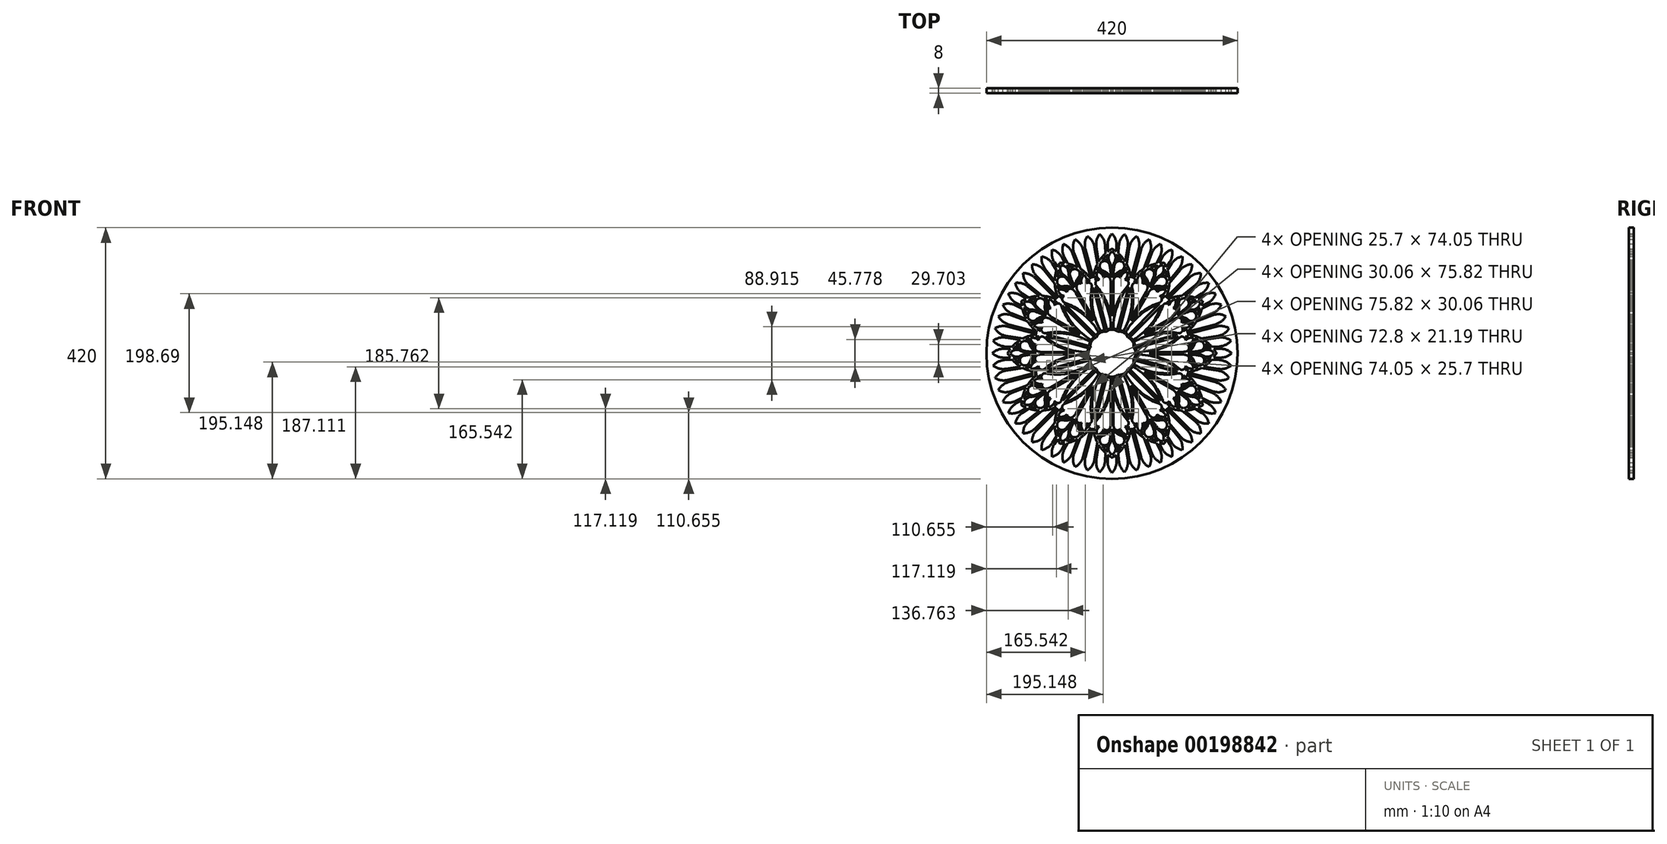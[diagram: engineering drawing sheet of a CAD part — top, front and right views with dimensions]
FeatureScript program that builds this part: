
annotation { "Feature Type Name" : "Feature", "Feature Type Description" : "" }
export const myFeature = defineFeature(function(context is Context, id is Id, definition is map)
    precondition{}
    {
        {
            var Q0;
            Q0=qCreatedBy(makeId("Front.planeOp"),FACE);
            var sketch = newSketch(context, id + "F0", { "sketchPlane" : qUnion([Q0])});
            skLineSegment(sketch, "E0", {"start": v(0, 0) * mm, "end": v(58.1, 216.81) * mm, "construction": true});
            skLineSegment(sketch, "E1", {"start": v(-11.54, 220.15) * mm, "end": v(-2.06, 39.35) * mm, "construction": true});
            skLineSegment(sketch, "E2", {"start": v(0, 220.15) * mm, "end": v(0, 0) * mm, "construction": true});
            skLineSegment(sketch, "E3", {"start": v(0, 0) * mm, "end": v(-33.6, 212.18) * mm, "construction": true});
            skLineSegment(sketch, "E4", {"start": v(0, 0) * mm, "end": v(-7.9, 37.16) * mm, "construction": true});
            skCircle(sketch, "E5", {"center": v(0, 0) * mm, "radius": 200 * mm, "construction": true});
            skCircle(sketch, "E6", {"center": v(0, 0) * mm, "radius": 180 * mm, "construction": true});
            skLineSegment(sketch, "E7", {"start": v(0, 0) * mm, "end": v(-57.94, 216.22) * mm, "construction": true});
            skCircle(sketch, "E8", {"center": v(0, 0) * mm, "radius": 25 * mm, "construction": true});
            skCircle(sketch, "E9", {"center": v(-21.65, 12.5) * mm, "radius": 12.5 * mm, "construction": true});
            skCircle(sketch, "E10", {"center": v(21.65, 12.5) * mm, "radius": 12.5 * mm, "construction": true});
            skCircle(sketch, "E11", {"center": v(21.65, -12.5) * mm, "radius": 12.5 * mm, "construction": true});
            skCircle(sketch, "E12", {"center": v(0, -25) * mm, "radius": 12.5 * mm, "construction": true});
            skCircle(sketch, "E13", {"center": v(-21.65, -12.5) * mm, "radius": 12.5 * mm, "construction": true});
            skLineSegment(sketch, "E14", {"start": v(-25.79, 103.96) * mm, "end": v(-8.43, 39.18) * mm});
            skArc(sketch, "E15", {"start": v(-6.74, 165.04) * mm, "mid": v(-11.52, 160.5) * mm, "end": v(-15.77, 155.46) * mm});
            skArc(sketch, "E16", {"start": v(0, 174.68) * mm, "mid": v(-3.53, 172.47) * mm, "end": v(-6.9, 170.05) * mm});
            skLineSegment(sketch, "E17", {"start": v(-44.65, 174.37) * mm, "end": v(-31.54, 125.45) * mm});
            skLineSegment(sketch, "E18", {"start": v(-29.15, 177.62) * mm, "end": v(-24.6, 148.94) * mm});
            skArc(sketch, "E19", {"start": v(-41.58, 195.63) * mm, "mid": v(-45.3, 185.32) * mm, "end": v(-44.65, 174.37) * mm});
            skArc(sketch, "E20", {"start": v(-29.15, 177.62) * mm, "mid": v(-33.32, 188.04) * mm, "end": v(-41.58, 195.63) * mm});
            skLineSegment(sketch, "E21", {"start": v(-22.23, 153.11) * mm, "end": v(-26.18, 178.09) * mm});
            skLineSegment(sketch, "E22", {"start": v(-10.75, 166.85) * mm, "end": v(-11.42, 179.64) * mm});
            skArc(sketch, "E23", {"start": v(-20.9, 198.9) * mm, "mid": v(-25.68, 189.04) * mm, "end": v(-26.18, 178.09) * mm});
            skArc(sketch, "E24", {"start": v(-11.42, 179.64) * mm, "mid": v(-14.18, 190.25) * mm, "end": v(-20.9, 198.9) * mm});
            skArc(sketch, "E25.trimOffspring", {"start": v(-24.6, 148.94) * mm, "mid": v(-29.21, 137.53) * mm, "end": v(-31.54, 125.45) * mm});
            skArc(sketch, "E26.trimOffspring", {"start": v(-10.75, 166.85) * mm, "mid": v(-16.97, 160.39) * mm, "end": v(-22.23, 153.11) * mm});
            skLineSegment(sketch, "E27", {"start": v(-6.9, 170.05) * mm, "end": v(-7.42, 179.85) * mm});
            skArc(sketch, "E28", {"start": v(0, 200) * mm, "mid": v(-5.78, 190.69) * mm, "end": v(-7.42, 179.85) * mm});
            skLineSegment(sketch, "E29.MirrorCS", {"start": v(6.9, 170.05) * mm, "end": v(7.42, 179.85) * mm});
            skLineSegment(sketch, "E30.MirrorCS", {"start": v(25.79, 103.96) * mm, "end": v(8.43, 39.18) * mm});
            skArc(sketch, "E31.MirrorCS", {"start": v(6.74, 165.04) * mm, "mid": v(11.52, 160.5) * mm, "end": v(15.77, 155.46) * mm});
            skArc(sketch, "E32.MirrorCS", {"start": v(0, 174.68) * mm, "mid": v(3.53, 172.47) * mm, "end": v(6.9, 170.05) * mm});
            skArc(sketch, "E33.MirrorCS", {"start": v(0, 200) * mm, "mid": v(5.78, 190.69) * mm, "end": v(7.42, 179.85) * mm});
            skArc(sketch, "E34.MirrorCS", {"start": v(11.42, 179.64) * mm, "mid": v(14.18, 190.25) * mm, "end": v(20.9, 198.9) * mm});
            skArc(sketch, "E35.MirrorCS", {"start": v(20.9, 198.9) * mm, "mid": v(25.68, 189.04) * mm, "end": v(26.18, 178.09) * mm});
            skLineSegment(sketch, "E36.MirrorCS", {"start": v(22.23, 153.11) * mm, "end": v(26.18, 178.09) * mm});
            skArc(sketch, "E37.MirrorCS", {"start": v(10.75, 166.85) * mm, "mid": v(16.97, 160.39) * mm, "end": v(22.23, 153.11) * mm});
            skLineSegment(sketch, "E38.MirrorCS", {"start": v(10.75, 166.85) * mm, "end": v(11.42, 179.64) * mm});
            skArc(sketch, "E39.MirrorCS", {"start": v(29.15, 177.62) * mm, "mid": v(33.32, 188.04) * mm, "end": v(41.58, 195.63) * mm});
            skArc(sketch, "E40.MirrorCS", {"start": v(41.58, 195.63) * mm, "mid": v(45.3, 185.32) * mm, "end": v(44.65, 174.37) * mm});
            skLineSegment(sketch, "E41.MirrorCS", {"start": v(44.65, 174.37) * mm, "end": v(31.54, 125.45) * mm});
            skArc(sketch, "E42.MirrorCS", {"start": v(24.6, 148.94) * mm, "mid": v(29.21, 137.53) * mm, "end": v(31.54, 125.45) * mm});
            skLineSegment(sketch, "E43.MirrorCS", {"start": v(29.15, 177.62) * mm, "end": v(24.6, 148.94) * mm});
            skArc(sketch, "E44", {"start": v(-2, 117.52) * mm, "mid": v(-2.4, 121.45) * mm, "end": v(-3.6, 125.22) * mm});
            skLineSegment(sketch, "E45", {"start": v(-23.62, 111.14) * mm, "end": v(-23.62, 111.14) * mm});
            skCircle(sketch, "E46", {"center": v(-21.76, 116.84) * mm, "radius": 8 * mm, "construction": true});
            skCircle(sketch, "E47", {"center": v(-20.62, 130.8) * mm, "radius": 6 * mm, "construction": true});
            skCircle(sketch, "E48", {"center": v(-20.62, 130.8) * mm, "radius": 8 * mm, "construction": true});
            skArc(sketch, "E49", {"start": v(-3.6, 125.22) * mm, "mid": v(-8.52, 128.8) * mm, "end": v(-14.04, 126.24) * mm});
            skCircle(sketch, "E50", {"center": v(-9.1, 122.82) * mm, "radius": 8 * mm, "construction": true});
            skLineSegment(sketch, "E51", {"start": v(-21.76, 116.84) * mm, "end": v(-9.1, 122.82) * mm, "construction": true});
            skPoint(sketch, "E52", {"position": v(-15.43, 119.83) * mm});
            skArc(sketch, "E53", {"start": v(-2, 126.53) * mm, "mid": v(-11.34, 136.34) * mm, "end": v(-24.7, 138.54) * mm});
            skArc(sketch, "E54", {"start": v(-2, 41.38) * mm, "mid": v(-8.5, 78.35) * mm, "end": v(-27.2, 110.9) * mm});
            skArc(sketch, "E55", {"start": v(-25.38, 136.37) * mm, "mid": v(-25.35, 128.98) * mm, "end": v(-21.27, 122.82) * mm});
            skArc(sketch, "E56", {"start": v(-14.04, 126.24) * mm, "mid": v(-18.1, 133.11) * mm, "end": v(-25.38, 136.37) * mm});
            skArc(sketch, "E57.MirrorCS", {"start": v(2, 126.53) * mm, "mid": v(11.34, 136.34) * mm, "end": v(24.7, 138.54) * mm});
            skArc(sketch, "E58.MirrorCS", {"start": v(2, 117.52) * mm, "mid": v(2.4, 121.45) * mm, "end": v(3.6, 125.22) * mm});
            skCircle(sketch, "E59.MirrorC", {"center": v(9.1, 122.82) * mm, "radius": 8 * mm, "construction": true});
            skArc(sketch, "E60.MirrorC", {"start": v(3.6, 125.22) * mm, "mid": v(8.52, 128.8) * mm, "end": v(14.04, 126.24) * mm});
            skCircle(sketch, "E61.MirrorC", {"center": v(20.62, 130.8) * mm, "radius": 8 * mm, "construction": true});
            skCircle(sketch, "E62.MirrorC", {"center": v(21.76, 116.84) * mm, "radius": 8 * mm, "construction": true});
            skArc(sketch, "E63.MirrorC", {"start": v(21.27, 122.82) * mm, "mid": v(27.14, 119.5) * mm, "end": v(26.2, 112.8) * mm});
            skArc(sketch, "E64.MirrorCS", {"start": v(14.04, 126.24) * mm, "mid": v(18.1, 133.11) * mm, "end": v(25.38, 136.37) * mm});
            skArc(sketch, "E65.MirrorCS", {"start": v(25.38, 136.37) * mm, "mid": v(25.35, 128.98) * mm, "end": v(21.27, 122.82) * mm});
            skArc(sketch, "E66.MirrorCS", {"start": v(2, 41.38) * mm, "mid": v(8.5, 78.35) * mm, "end": v(27.2, 110.9) * mm});
            skArc(sketch, "E67.trimOffspring", {"start": v(-21.27, 122.82) * mm, "mid": v(-27.14, 119.5) * mm, "end": v(-26.2, 112.8) * mm});
            skArc(sketch, "E68.trimOffspring", {"start": v(27.2, 110.9) * mm, "mid": v(26.6, 107.4) * mm, "end": v(25.79, 103.96) * mm});
            skPoint(sketch, "E69.trimOffspring.start.orphan", {"position": v(25.38, 136.37) * mm});
            skArc(sketch, "E70", {"start": v(-2, 62.32) * mm, "mid": v(-7.87, 101.18) * mm, "end": v(-25.38, 136.37) * mm, "construction": true});
            skArc(sketch, "E71.trimOffspring", {"start": v(-27.2, 110.9) * mm, "mid": v(-26.6, 107.4) * mm, "end": v(-25.79, 103.96) * mm});
            skPoint(sketch, "E72.orphan", {"position": v(-27.85, 111.66) * mm});
            skPoint(sketch, "E73.orphan", {"position": v(27.85, 111.66) * mm});
            skArc(sketch, "E74", {"start": v(-24.7, 138.54) * mm, "mid": v(-27.58, 124.86) * mm, "end": v(-27.2, 110.9) * mm, "construction": true});
            skArc(sketch, "E75", {"start": v(-3.6, 125.22) * mm, "mid": v(-12.5, 134.69) * mm, "end": v(-25.38, 136.37) * mm, "construction": true});
            skLineSegment(sketch, "E76", {"start": v(-26.85, 123.32) * mm, "end": v(-13.01, 132.72) * mm, "construction": true});
            skPoint(sketch, "E77", {"position": v(-19.93, 128.02) * mm});
            skLineSegment(sketch, "E78", {"start": v(0, 0) * mm, "end": v(-23.14, 220.12) * mm, "construction": true});
            skArc(sketch, "E79", {"start": v(-13.14, 129.73) * mm, "mid": v(-15.93, 133.8) * mm, "end": v(-19.89, 136.76) * mm});
            skArc(sketch, "E80", {"start": v(-7.08, 130.56) * mm, "mid": v(-12.9, 134.88) * mm, "end": v(-19.89, 136.76) * mm});
            skArc(sketch, "E81", {"start": v(-7.08, 130.56) * mm, "mid": v(-10.2, 130.75) * mm, "end": v(-13.14, 129.73) * mm});
            skArc(sketch, "E82", {"start": v(-27.19, 128.15) * mm, "mid": v(-26.32, 126.04) * mm, "end": v(-25.15, 124.09) * mm});
            skArc(sketch, "E83", {"start": v(-27.19, 128.15) * mm, "mid": v(-27.55, 125.15) * mm, "end": v(-27.77, 122.13) * mm});
            skArc(sketch, "E84.MirrorCS", {"start": v(7.08, 130.56) * mm, "mid": v(12.9, 134.88) * mm, "end": v(19.89, 136.76) * mm});
            skArc(sketch, "E85.MirrorCS", {"start": v(13.14, 129.73) * mm, "mid": v(15.93, 133.8) * mm, "end": v(19.89, 136.76) * mm});
            skArc(sketch, "E86.MirrorCS", {"start": v(7.08, 130.56) * mm, "mid": v(10.2, 130.75) * mm, "end": v(13.14, 129.73) * mm});
            skArc(sketch, "E87.MirrorCS", {"start": v(27.19, 128.15) * mm, "mid": v(26.32, 126.04) * mm, "end": v(25.15, 124.09) * mm});
            skArc(sketch, "E88.MirrorCS", {"start": v(27.19, 128.15) * mm, "mid": v(27.55, 125.15) * mm, "end": v(27.77, 122.13) * mm});
            skArc(sketch, "E89", {"start": v(-25.15, 124.09) * mm, "mid": v(-26.56, 123.24) * mm, "end": v(-27.77, 122.13) * mm});
            skArc(sketch, "E90.MirrorCS", {"start": v(25.15, 124.09) * mm, "mid": v(26.56, 123.24) * mm, "end": v(27.77, 122.13) * mm});
            skCircle(sketch, "E91", {"center": v(0, 159.8) * mm, "radius": 10.33 * mm, "construction": true});
            skCircle(sketch, "E92", {"center": v(0, 159.8) * mm, "radius": 8.33 * mm, "construction": true});
            skCircle(sketch, "E93", {"center": v(12.28, 145.74) * mm, "radius": 10.33 * mm, "construction": true});
            skCircle(sketch, "E94", {"center": v(-12.28, 145.74) * mm, "radius": 8.33 * mm, "construction": true});
            skCircle(sketch, "E95", {"center": v(-12.28, 145.74) * mm, "radius": 10.33 * mm, "construction": true});
            skArc(sketch, "E96", {"start": v(0, 126.53) * mm, "mid": v(-0.54, 137.22) * mm, "end": v(-2.16, 147.8) * mm});
            skArc(sketch, "E97", {"start": v(-2, 126.53) * mm, "mid": v(-2.53, 137.02) * mm, "end": v(-4.12, 147.4) * mm});
            skArc(sketch, "E98", {"start": v(-2.16, 147.8) * mm, "mid": v(-2.88, 150.23) * mm, "end": v(-4.02, 152.5) * mm});
            skArc(sketch, "E99", {"start": v(0, 170) * mm, "mid": v(-5.61, 162.07) * mm, "end": v(-4.02, 152.5) * mm});
            skArc(sketch, "E100", {"start": v(-4.12, 147.4) * mm, "mid": v(-17.85, 151.94) * mm, "end": v(-14.81, 137.8) * mm});
            skArc(sketch, "E101", {"start": v(-6.74, 165.04) * mm, "mid": v(-7.92, 159.95) * mm, "end": v(-7.24, 154.76) * mm});
            skArc(sketch, "E102", {"start": v(-7.24, 154.76) * mm, "mid": v(-11.43, 156.03) * mm, "end": v(-15.77, 155.46) * mm});
            skArc(sketch, "E103", {"start": v(-22.49, 144.15) * mm, "mid": v(-21.6, 141.27) * mm, "end": v(-19.9, 138.76) * mm});
            skArc(sketch, "E104.trimOffspring", {"start": v(-22.49, 144.15) * mm, "mid": v(-23.66, 141.37) * mm, "end": v(-24.7, 138.54) * mm});
            skArc(sketch, "E105.MirrorCS", {"start": v(0, 170) * mm, "mid": v(5.61, 162.07) * mm, "end": v(4.02, 152.5) * mm});
            skArc(sketch, "E106.MirrorCS", {"start": v(6.74, 165.04) * mm, "mid": v(7.92, 159.95) * mm, "end": v(7.24, 154.76) * mm});
            skCircle(sketch, "E107.MirrorC", {"center": v(12.28, 145.74) * mm, "radius": 8.33 * mm, "construction": true});
            skArc(sketch, "E108.MirrorCS", {"start": v(7.24, 154.76) * mm, "mid": v(11.43, 156.03) * mm, "end": v(15.77, 155.46) * mm});
            skArc(sketch, "E109.MirrorCS", {"start": v(2, 126.53) * mm, "mid": v(2.53, 137.02) * mm, "end": v(4.12, 147.4) * mm});
            skArc(sketch, "E110.MirrorCS", {"start": v(0, 126.53) * mm, "mid": v(0.54, 137.22) * mm, "end": v(2.16, 147.8) * mm});
            skArc(sketch, "E111.MirrorCS", {"start": v(2.16, 147.8) * mm, "mid": v(2.88, 150.23) * mm, "end": v(4.02, 152.5) * mm});
            skArc(sketch, "E112.MirrorCS", {"start": v(22.49, 144.15) * mm, "mid": v(21.6, 141.27) * mm, "end": v(19.9, 138.76) * mm});
            skArc(sketch, "E113.MirrorCS", {"start": v(4.12, 147.4) * mm, "mid": v(17.85, 151.94) * mm, "end": v(14.81, 137.8) * mm});
            skArc(sketch, "E114.trimOffspring", {"start": v(22.49, 144.15) * mm, "mid": v(23.66, 141.37) * mm, "end": v(24.7, 138.54) * mm});
            skPoint(sketch, "E115.orphan", {"position": v(0, 170) * mm});
            skPoint(sketch, "E116.orphan", {"position": v(0, 117.52) * mm});
            skLineSegment(sketch, "E117", {"start": v(-2, 117.52) * mm, "end": v(-2, 126.53) * mm, "construction": true});
            skArc(sketch, "E118.trimOffspring", {"start": v(-2, 62.32) * mm, "mid": v(-10.85, 89.12) * mm, "end": v(-26.2, 112.8) * mm});
            skLineSegment(sketch, "E119.trimOffspring", {"start": v(-2, 62.32) * mm, "end": v(-2, 117.52) * mm});
            skArc(sketch, "E120.trimOffspring", {"start": v(2, 62.32) * mm, "mid": v(10.85, 89.12) * mm, "end": v(26.2, 112.8) * mm});
            skCircle(sketch, "E121", {"center": v(0, 25) * mm, "radius": 14.5 * mm, "construction": true});
            skLineSegment(sketch, "E122.trimOffspring", {"start": v(2, 62.32) * mm, "end": v(2, 117.52) * mm});
            skLineSegment(sketch, "E123.trimOffspring", {"start": v(-1.96, 37.35) * mm, "end": v(0, 0) * mm, "construction": true});
            skCircle(sketch, "E124", {"center": v(0, 25) * mm, "radius": 12.5 * mm, "construction": true});
            skCircle(sketch, "E125", {"center": v(0, 25) * mm, "radius": 16.5 * mm, "construction": true});
            skLineSegment(sketch, "E126.trimOffspring", {"start": v(-7.95, 37.38) * mm, "end": v(-45.1, 212.18) * mm, "construction": true});
            skArc(sketch, "E127", {"start": v(-2, 41.38) * mm, "mid": v(-5.33, 40.62) * mm, "end": v(-8.43, 39.18) * mm});
            skArc(sketch, "E128", {"start": v(8.43, 39.18) * mm, "mid": v(5.33, 40.62) * mm, "end": v(2, 41.38) * mm});
            skLineSegment(sketch, "E129", {"start": v(-2, 34.24) * mm, "end": v(-2, 41.38) * mm, "construction": true});
            skLineSegment(sketch, "E130", {"start": v(-9.6, 35.86) * mm, "end": v(-54.35, 202.84) * mm});
            skLineSegment(sketch, "E131", {"start": v(54.35, 202.84) * mm, "end": v(9.6, 35.86) * mm});
            skArc(sketch, "E132", {"start": v(9.6, 35.86) * mm, "mid": v(0, 39.5) * mm, "end": v(-9.6, 35.86) * mm});
            skArc(sketch, "E133", {"start": v(54.35, 202.84) * mm, "mid": v(0, 210) * mm, "end": v(-54.35, 202.84) * mm});
            skSolve(sketch);
        }
        {
            var Q0;
            Q0=makeQuery(id+"F0.imprint","IMPRINT",FACE,{"disambiguationData":[TD([[makeQuery(id+"F0.imprint","IMPRINT",EDGE,{"derivedFrom":sQuery(id+"F0.wireOp",EDGE,"E14")}),-1.0]])]});
            extrude(context, id + "F1", {"entities" : qUnion([Q0]), "depth" : 8 * mm});
        }
        {
            var Q0;
            Q0=makeQuery(id+"F1.opExtrude","SWEPT_BODY",BODY,{"disambiguationData":[OSD([sQuery(id+"F0.wireOp",EDGE,"E14"),sQuery(id+"F0.wireOp",EDGE,"E15"),sQuery(id+"F0.wireOp",EDGE,"E16"),sQuery(id+"F0.wireOp",EDGE,"E17"),sQuery(id+"F0.wireOp",EDGE,"E18"),sQuery(id+"F0.wireOp",EDGE,"E19"),sQuery(id+"F0.wireOp",EDGE,"E20"),sQuery(id+"F0.wireOp",EDGE,"E21"),sQuery(id+"F0.wireOp",EDGE,"E22"),sQuery(id+"F0.wireOp",EDGE,"E23"),sQuery(id+"F0.wireOp",EDGE,"E24"),sQuery(id+"F0.wireOp",EDGE,"E25.trimOffspring"),sQuery(id+"F0.wireOp",EDGE,"E26.trimOffspring"),sQuery(id+"F0.wireOp",EDGE,"E27"),sQuery(id+"F0.wireOp",EDGE,"E28"),sQuery(id+"F0.wireOp",EDGE,"E29.MirrorCS"),sQuery(id+"F0.wireOp",EDGE,"E30.MirrorCS"),sQuery(id+"F0.wireOp",EDGE,"E32.MirrorCS"),sQuery(id+"F0.wireOp",EDGE,"E33.MirrorCS"),sQuery(id+"F0.wireOp",EDGE,"E34.MirrorCS"),sQuery(id+"F0.wireOp",EDGE,"E35.MirrorCS"),sQuery(id+"F0.wireOp",EDGE,"E36.MirrorCS"),sQuery(id+"F0.wireOp",EDGE,"E37.MirrorCS"),sQuery(id+"F0.wireOp",EDGE,"E38.MirrorCS"),sQuery(id+"F0.wireOp",EDGE,"E39.MirrorCS"),sQuery(id+"F0.wireOp",EDGE,"E40.MirrorCS"),sQuery(id+"F0.wireOp",EDGE,"E41.MirrorCS"),sQuery(id+"F0.wireOp",EDGE,"E42.MirrorCS"),sQuery(id+"F0.wireOp",EDGE,"E43.MirrorCS"),sQuery(id+"F0.wireOp",EDGE,"E44"),sQuery(id+"F0.wireOp",EDGE,"E49"),sQuery(id+"F0.wireOp",EDGE,"E53"),sQuery(id+"F0.wireOp",EDGE,"E54"),sQuery(id+"F0.wireOp",EDGE,"E55"),sQuery(id+"F0.wireOp",EDGE,"E56"),sQuery(id+"F0.wireOp",EDGE,"E57.MirrorCS"),sQuery(id+"F0.wireOp",EDGE,"E58.MirrorCS"),sQuery(id+"F0.wireOp",EDGE,"E60.MirrorC"),sQuery(id+"F0.wireOp",EDGE,"E63.MirrorC"),sQuery(id+"F0.wireOp",EDGE,"E64.MirrorCS"),sQuery(id+"F0.wireOp",EDGE,"E65.MirrorCS"),sQuery(id+"F0.wireOp",EDGE,"E66.MirrorCS"),sQuery(id+"F0.wireOp",EDGE,"E67.trimOffspring"),sQuery(id+"F0.wireOp",EDGE,"E68.trimOffspring"),sQuery(id+"F0.wireOp",EDGE,"E71.trimOffspring"),sQuery(id+"F0.wireOp",EDGE,"E79"),sQuery(id+"F0.wireOp",EDGE,"E80"),sQuery(id+"F0.wireOp",EDGE,"E81"),sQuery(id+"F0.wireOp",EDGE,"E82"),sQuery(id+"F0.wireOp",EDGE,"E83"),sQuery(id+"F0.wireOp",EDGE,"E84.MirrorCS"),sQuery(id+"F0.wireOp",EDGE,"E85.MirrorCS"),sQuery(id+"F0.wireOp",EDGE,"E86.MirrorCS"),sQuery(id+"F0.wireOp",EDGE,"E89"),sQuery(id+"F0.wireOp",EDGE,"E87.MirrorCS"),sQuery(id+"F0.wireOp",EDGE,"E88.MirrorCS"),sQuery(id+"F0.wireOp",EDGE,"E90.MirrorCS"),sQuery(id+"F0.wireOp",EDGE,"E96"),sQuery(id+"F0.wireOp",EDGE,"E97"),sQuery(id+"F0.wireOp",EDGE,"E98"),sQuery(id+"F0.wireOp",EDGE,"E99"),sQuery(id+"F0.wireOp",EDGE,"E100"),sQuery(id+"F0.wireOp",EDGE,"E101"),sQuery(id+"F0.wireOp",EDGE,"E102"),sQuery(id+"F0.wireOp",EDGE,"E103"),sQuery(id+"F0.wireOp",EDGE,"E104.trimOffspring"),sQuery(id+"F0.wireOp",EDGE,"E105.MirrorCS"),sQuery(id+"F0.wireOp",EDGE,"E106.MirrorCS"),sQuery(id+"F0.wireOp",EDGE,"E108.MirrorCS"),sQuery(id+"F0.wireOp",EDGE,"E31.MirrorCS"),sQuery(id+"F0.wireOp",EDGE,"E109.MirrorCS"),sQuery(id+"F0.wireOp",EDGE,"E110.MirrorCS"),sQuery(id+"F0.wireOp",EDGE,"E111.MirrorCS"),sQuery(id+"F0.wireOp",EDGE,"E112.MirrorCS"),sQuery(id+"F0.wireOp",EDGE,"E113.MirrorCS"),sQuery(id+"F0.wireOp",EDGE,"E114.trimOffspring"),sQuery(id+"F0.wireOp",EDGE,"E118.trimOffspring"),sQuery(id+"F0.wireOp",EDGE,"E119.trimOffspring"),sQuery(id+"F0.wireOp",EDGE,"E120.trimOffspring"),sQuery(id+"F0.wireOp",EDGE,"E122.trimOffspring"),sQuery(id+"F0.wireOp",EDGE,"E127"),sQuery(id+"F0.wireOp",EDGE,"E128"),sQuery(id+"F0.wireOp",EDGE,"E130"),sQuery(id+"F0.wireOp",EDGE,"E131"),sQuery(id+"F0.wireOp",EDGE,"E132"),sQuery(id+"F0.wireOp",EDGE,"E133")])]});
            var Q1;
            Q1=sQuery(id+"F0.wireOp",EDGE,"E6");
            circularPattern(context, id + "F2", {"operationType" : NewBodyOperationType.ADD, "entities" : qUnion([Q0]), "axis" : qUnion([Q1]), "angle" : 360 * degree, "instanceCount" : 12, "equalSpace" : true});
        }
    });
